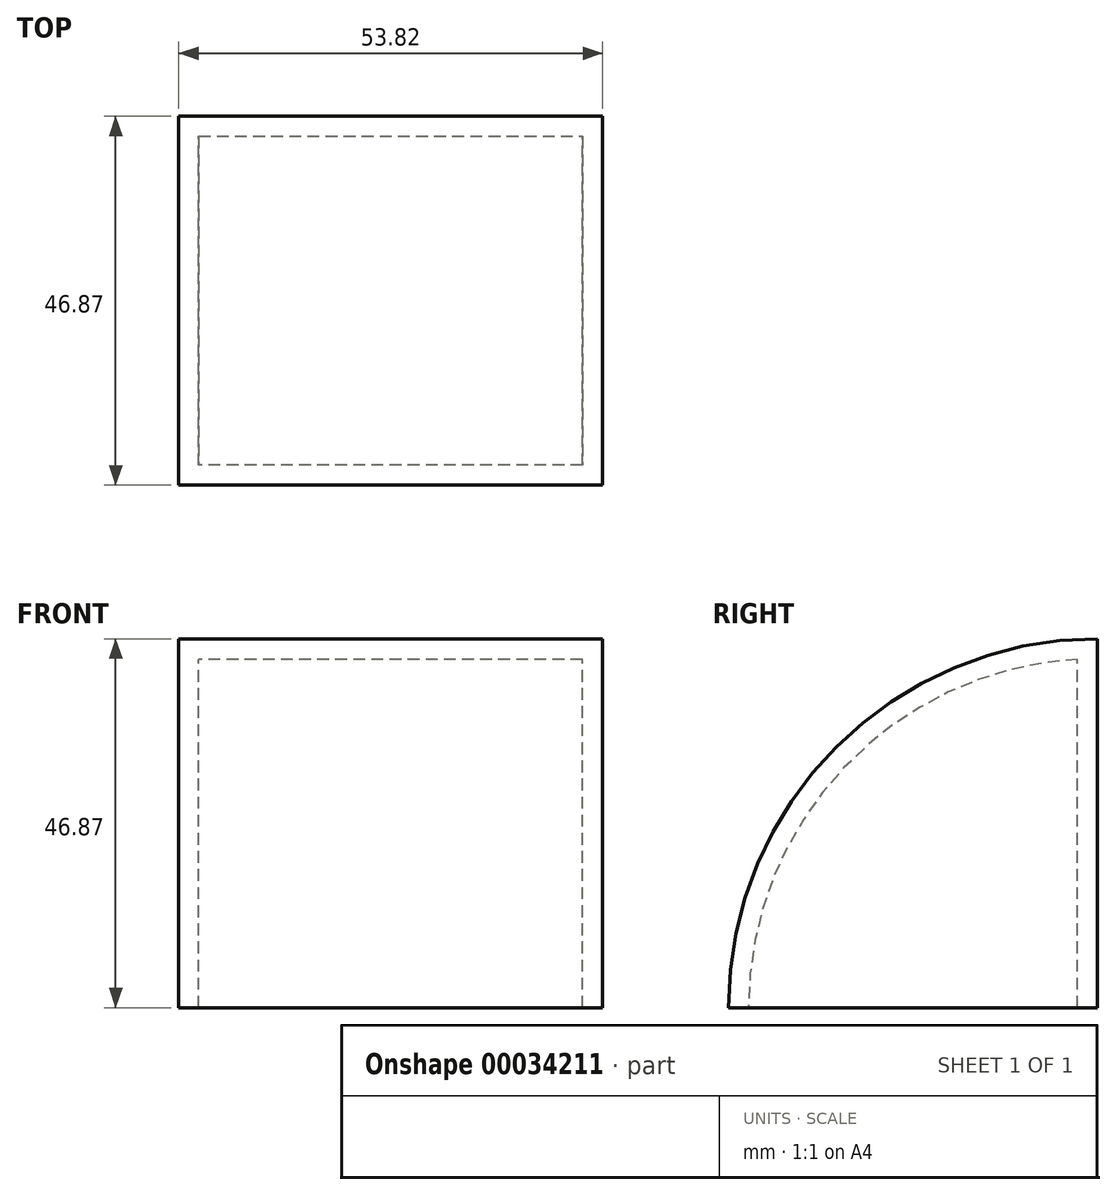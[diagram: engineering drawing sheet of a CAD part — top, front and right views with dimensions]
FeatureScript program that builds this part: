
annotation { "Feature Type Name" : "Feature", "Feature Type Description" : "" }
export const myFeature = defineFeature(function(context is Context, id is Id, definition is map)
    precondition{}
    {
        {
            var Q0;
            Q0=qCreatedBy(makeId("Front.planeOp"),FACE);
            var sketch = newSketch(context, id + "F0", { "sketchPlane" : qUnion([Q0])});
            skLineSegment(sketch, "E0.bottom", {"start": v(0, 0) * mm, "end": v(53.82, 0) * mm});
            skLineSegment(sketch, "E0.top", {"start": v(0, 46.87) * mm, "end": v(53.82, 46.87) * mm});
            skLineSegment(sketch, "E0.left", {"start": v(0, 0) * mm, "end": v(0, 46.87) * mm});
            skLineSegment(sketch, "E0.right", {"start": v(53.82, 0) * mm, "end": v(53.82, 46.87) * mm});
            skSolve(sketch);
        }
        {
            var Q0;
            Q0 = qSketchRegion(id + "F0", true);
            var Q1;
            Q1=sQuery(id+"F0.wireOp",EDGE,"E0.bottom");
            revolve(context, id + "F1", {"entities" : qUnion([Q0]), "axis" : qUnion([Q1]), "revolveType" : RevolveType.ONE_DIRECTION, "angle" : 90 * degree});
        }
        {
            var Q0;
            Q0=makeQuery(id+"F1.opRevolve","CAP_FACE",FACE,{"disambiguationData":[OSD([sQuery(id+"F0.wireOp",EDGE,"E0.bottom"),sQuery(id+"F0.wireOp",EDGE,"E0.top"),sQuery(id+"F0.wireOp",EDGE,"E0.left"),sQuery(id+"F0.wireOp",EDGE,"E0.right")])],"isStart":false});
            shell(context, id + "F2", {"entities" : qUnion([Q0]), "thickness" : 2.54 * mm});
        }
    });
